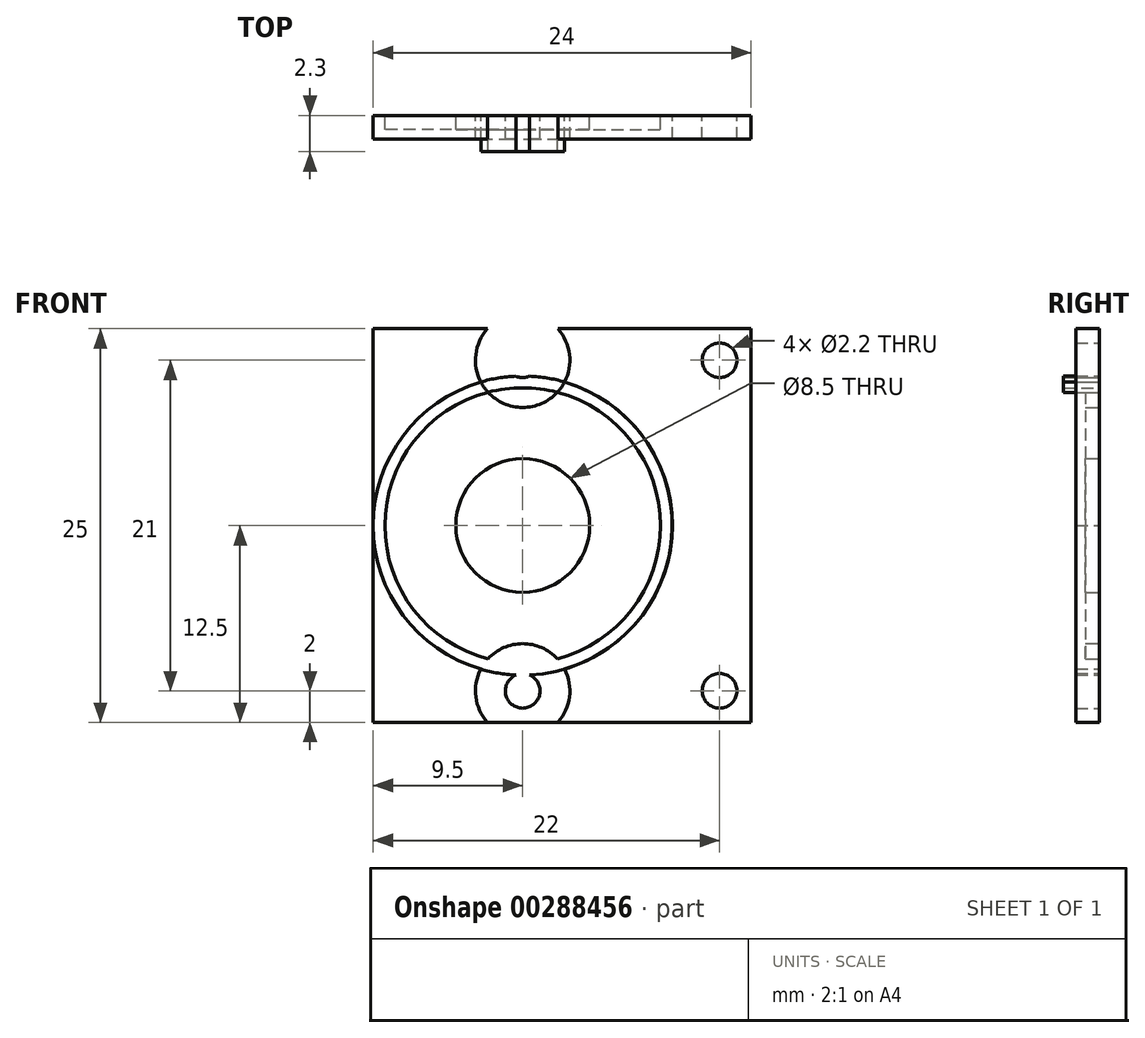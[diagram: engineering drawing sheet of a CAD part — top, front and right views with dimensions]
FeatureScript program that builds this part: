
annotation { "Feature Type Name" : "Feature", "Feature Type Description" : "" }
export const myFeature = defineFeature(function(context is Context, id is Id, definition is map)
    precondition{}
    {
        {
            var Q0;
            Q0=qCreatedBy(makeId("Front.planeOp"),FACE);
            var sketch = newSketch(context, id + "F0", { "sketchPlane" : qUnion([Q0])});
            skLineSegment(sketch, "E0.bottom", {"start": v(-12, 12.5) * mm, "end": v(12, 12.5) * mm});
            skLineSegment(sketch, "E0.top", {"start": v(-12, -12.5) * mm, "end": v(12, -12.5) * mm});
            skLineSegment(sketch, "E0.left", {"start": v(-12, 12.5) * mm, "end": v(-12, -12.5) * mm});
            skLineSegment(sketch, "E0.right", {"start": v(12, 12.5) * mm, "end": v(12, -12.5) * mm});
            skPoint(sketch, "E0.middle", {"position": v(0, 0) * mm});
            skCircle(sketch, "E1", {"center": v(-2.5, 0) * mm, "radius": 4.25 * mm});
            skCircle(sketch, "E2", {"center": v(10, 10.5) * mm, "radius": 1.1 * mm});
            skCircle(sketch, "E3", {"center": v(10, -10.5) * mm, "radius": 1.1 * mm});
            skCircle(sketch, "E4", {"center": v(-2.5, -10.5) * mm, "radius": 1.1 * mm});
            skCircle(sketch, "E5", {"center": v(-2.5, 10.5) * mm, "radius": 1.1 * mm});
            skCircle(sketch, "E6", {"center": v(-2.5, 0) * mm, "radius": 8.75 * mm});
            skCircle(sketch, "E7", {"center": v(-2.5, 0) * mm, "radius": 9.5 * mm});
            skCircle(sketch, "E8", {"center": v(-2.5, 10.5) * mm, "radius": 3 * mm});
            skCircle(sketch, "E9", {"center": v(-2.5, -10.5) * mm, "radius": 3 * mm});
            skSolve(sketch);
        }
        {
            var Q0;
            {var subQ0=sQuery(id+"F0.wireOp",EDGE,"E0.left");var subQ1=sQuery(id+"F0.wireOp",EDGE,"E0.bottom");var subQ2=makeQuery(id+"F0.imprint","INTERSECT",VERTEX,{"derivedFrom":[subQ1,subQ0]});Q0=makeQuery(id+"F0.imprint","IMPRINT",FACE,{"disambiguationData":[TD([[makeQuery(id+"F0.imprint","IMPRINT",EDGE,{"disambiguationData":[TD([[subQ2,-1.0]])],"derivedFrom":subQ1}),-1.0]])]});}
            var Q1;
            {var subQ0=sQuery(id+"F0.wireOp",EDGE,"E0.right");Q1=makeQuery(id+"F0.imprint","IMPRINT",FACE,{"disambiguationData":[TD([[makeQuery(id+"F0.imprint","IMPRINT",EDGE,{"derivedFrom":subQ0}),-1.0]])]});}
            var Q2;
            {var subQ0=sQuery(id+"F0.wireOp",EDGE,"E0.left");var subQ1=sQuery(id+"F0.wireOp",EDGE,"E0.top");var subQ2=makeQuery(id+"F0.imprint","INTERSECT",VERTEX,{"derivedFrom":[subQ1,subQ0]});Q2=makeQuery(id+"F0.imprint","IMPRINT",FACE,{"disambiguationData":[TD([[makeQuery(id+"F0.imprint","IMPRINT",EDGE,{"disambiguationData":[TD([[subQ2,-1.0]])],"derivedFrom":subQ1}),1.0]])]});}
            extrude(context, id + "F1", {"entities" : qUnion([Q0, Q1, Q2]), "depth" : 1.5 * mm, "offsetDistance" : 25 * mm});
        }
        {
            var Q0;
            {var subQ3=sQuery(id+"F0.wireOp",EDGE,"E8");var subQ7=sQuery(id+"F0.wireOp",EDGE,"E0.bottom");var subQ8=makeQuery(id+"F0.imprint","INTERSECT",VERTEX,{"disambiguationData":[OD(0.0)],"derivedFrom":[subQ7,subQ3]});Q0=makeQuery(id+"F0.imprint","IMPRINT",FACE,{"disambiguationData":[TD([[makeQuery(id+"F0.imprint","IMPRINT",EDGE,{"disambiguationData":[TD([[subQ8,-1.0]])],"derivedFrom":subQ7}),-1.0]])]});}
            var Q1;
            {var subQ3=sQuery(id+"F0.wireOp",EDGE,"E9");var subQ5=sQuery(id+"F0.wireOp",EDGE,"E0.top");var subQ6=makeQuery(id+"F0.imprint","INTERSECT",VERTEX,{"disambiguationData":[OD(0.0)],"derivedFrom":[subQ5,subQ3]});Q1=makeQuery(id+"F0.imprint","IMPRINT",FACE,{"disambiguationData":[TD([[makeQuery(id+"F0.imprint","IMPRINT",EDGE,{"disambiguationData":[TD([[subQ6,-1.0]])],"derivedFrom":subQ5}),1.0]])]});}
            var Q2;
            {var subQ0=sQuery(id+"F0.wireOp",EDGE,"E7");var subQ1=sQuery(id+"F0.wireOp",EDGE,"E5");var subQ8=makeQuery(id+"F0.imprint","INTERSECT",VERTEX,{"disambiguationData":[OD(0.0)],"derivedFrom":[subQ1,subQ0]});Q2=makeQuery(id+"F0.imprint","IMPRINT",FACE,{"disambiguationData":[TD([[makeQuery(id+"F0.imprint","IMPRINT",EDGE,{"disambiguationData":[TD([[subQ8,1.0]])],"derivedFrom":subQ1}),-1.0]])]});}
            var Q3;
            {var subQ0=sQuery(id+"F0.wireOp",EDGE,"E7");var subQ1=sQuery(id+"F0.wireOp",EDGE,"E4");var subQ2=makeQuery(id+"F0.imprint","INTERSECT",VERTEX,{"disambiguationData":[OD(0.0)],"derivedFrom":[subQ1,subQ0]});Q3=makeQuery(id+"F0.imprint","IMPRINT",FACE,{"disambiguationData":[TD([[makeQuery(id+"F0.imprint","IMPRINT",EDGE,{"disambiguationData":[TD([[subQ2,1.0]])],"derivedFrom":subQ1}),-1.0]])]});}
            extrude(context, id + "F2", {"entities" : qUnion([Q0, Q1, Q2, Q3]), "depth" : 1.5 * mm, "offsetDistance" : 25 * mm});
        }
        {
            var Q0;
            {var subQ0=sQuery(id+"F0.wireOp",EDGE,"E8");var subQ1=sQuery(id+"F0.wireOp",EDGE,"E6");var subQ2=makeQuery(id+"F0.imprint","INTERSECT",VERTEX,{"disambiguationData":[OD(0.0)],"derivedFrom":[subQ1,subQ0]});Q0=makeQuery(id+"F0.imprint","IMPRINT",FACE,{"disambiguationData":[TD([[makeQuery(id+"F0.imprint","IMPRINT",EDGE,{"disambiguationData":[TD([[subQ2,-1.0]])],"derivedFrom":subQ1}),-1.0]])]});}
            var Q1;
            {var subQ0=sQuery(id+"F0.wireOp",EDGE,"E8");var subQ1=sQuery(id+"F0.wireOp",EDGE,"E6");var subQ2=makeQuery(id+"F0.imprint","INTERSECT",VERTEX,{"disambiguationData":[OD(1.0)],"derivedFrom":[subQ1,subQ0]});Q1=makeQuery(id+"F0.imprint","IMPRINT",FACE,{"disambiguationData":[TD([[makeQuery(id+"F0.imprint","IMPRINT",EDGE,{"disambiguationData":[TD([[subQ2,1.0]])],"derivedFrom":subQ1}),-1.0]])]});}
            extrude(context, id + "F3", {"entities" : qUnion([Q0, Q1]), "depth" : 2.3 * mm, "offsetDistance" : 25 * mm});
        }
        {
            var Q0;
            Q0=makeQuery(id+"F0.imprint","IMPRINT",FACE,{"disambiguationData":[TD([[makeQuery(id+"F0.imprint","IMPRINT",EDGE,{"derivedFrom":sQuery(id+"F0.wireOp",EDGE,"E1")}),-1.0]])]});
            var Q1;
            {var subQ0=sQuery(id+"F0.wireOp",EDGE,"E8");var subQ1=sQuery(id+"F0.wireOp",EDGE,"E6");var subQ2=makeQuery(id+"F0.imprint","INTERSECT",VERTEX,{"disambiguationData":[OD(0.0)],"derivedFrom":[subQ1,subQ0]});Q1=makeQuery(id+"F0.imprint","IMPRINT",FACE,{"disambiguationData":[TD([[makeQuery(id+"F0.imprint","IMPRINT",EDGE,{"disambiguationData":[TD([[subQ2,1.0]])],"derivedFrom":subQ1}),1.0]])]});}
            var Q2;
            {var subQ0=sQuery(id+"F0.wireOp",EDGE,"E9");var subQ1=sQuery(id+"F0.wireOp",EDGE,"E6");var subQ2=makeQuery(id+"F0.imprint","INTERSECT",VERTEX,{"disambiguationData":[OD(0.0)],"derivedFrom":[subQ1,subQ0]});Q2=makeQuery(id+"F0.imprint","IMPRINT",FACE,{"disambiguationData":[TD([[makeQuery(id+"F0.imprint","IMPRINT",EDGE,{"disambiguationData":[TD([[subQ2,-1.0]])],"derivedFrom":subQ1}),1.0]])]});}
            extrude(context, id + "F4", {"entities" : qUnion([Q0, Q1, Q2]), "operationType" : NewBodyOperationType.ADD, "depth" : 0.9 * mm, "offsetDistance" : 25 * mm});
        }
    });
